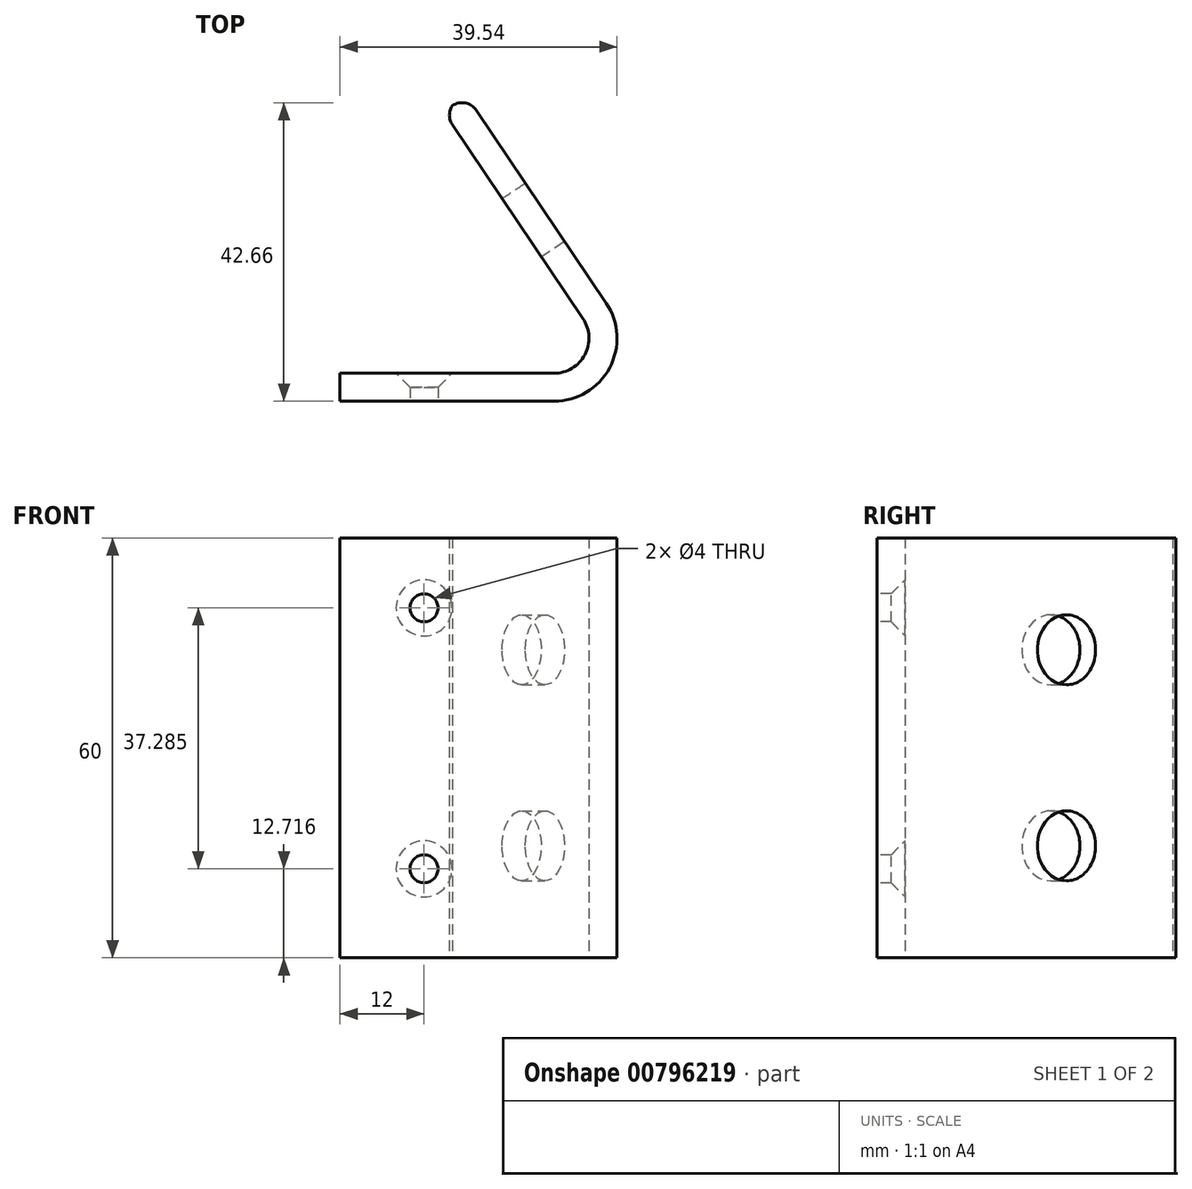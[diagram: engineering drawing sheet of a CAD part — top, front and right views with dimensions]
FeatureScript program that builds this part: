
annotation { "Feature Type Name" : "Feature", "Feature Type Description" : "" }
export const myFeature = defineFeature(function(context is Context, id is Id, definition is map)
    precondition{}
    {
        {
            var Q0;
            Q0=qCreatedBy(makeId("Top.planeOp"),FACE);
            var sketch = newSketch(context, id + "F0", { "sketchPlane" : qUnion([Q0])});
            skLineSegment(sketch, "E0", {"start": v(0, 0) * mm, "end": v(30.54, 0) * mm});
            skLineSegment(sketch, "E1", {"start": v(38.01, 14.02) * mm, "end": v(18.1, 43.63) * mm});
            skLineSegment(sketch, "E2", {"start": v(18.1, 43.63) * mm, "end": v(14.77, 41.4) * mm});
            skLineSegment(sketch, "E3", {"start": v(14.77, 41.4) * mm, "end": v(33.04, 14.25) * mm});
            skLineSegment(sketch, "E4", {"start": v(30.54, 4) * mm, "end": v(0, 4) * mm});
            skLineSegment(sketch, "E5", {"start": v(0, 4) * mm, "end": v(0, 0) * mm});
            skLineSegment(sketch, "E6", {"start": v(34.7, 11.8) * mm, "end": v(33.04, 14.25) * mm});
            skArc(sketch, "E7.filletArc", {"start": v(30.54, 4) * mm, "mid": v(34.96, 6.65) * mm, "end": v(34.7, 11.8) * mm});
            skPoint(sketch, "E8.visualSharp", {"position": v(45.54, 2.83) * mm});
            skPoint(sketch, "E9.visualSharp", {"position": v(50, 0) * mm});
            skPoint(sketch, "E10.newPointA", {"position": v(44.89, 3.8) * mm});
            skArc(sketch, "E10.filletArc", {"start": v(30.54, 0) * mm, "mid": v(38.49, 4.77) * mm, "end": v(38.01, 14.02) * mm});
            skSolve(sketch);
        }
        {
            var Q0;
            Q0=makeQuery(id+"F0.imprint","IMPRINT",FACE,{"disambiguationData":[TD([[makeQuery(id+"F0.imprint","IMPRINT",EDGE,{"derivedFrom":sQuery(id+"F0.wireOp",EDGE,"E0")}),1.0]])]});
            extrude(context, id + "F1", {"entities" : qUnion([Q0]), "depth" : 60 * mm, "offsetDistance" : 25 * mm});
        }
        {
            var Q0;
            Q0=makeQuery(id+"F1.opExtrude","SWEPT_FACE",FACE,{"disambiguationData":[OSD([sQuery(id+"F0.wireOp",EDGE,"E1")])]});
            var sketch = newSketch(context, id + "F2", { "sketchPlane" : qUnion([Q0])});
            skLineSegment(sketch, "E11", {"start": v(6.1, -8.7) * mm, "end": v(6.1, 93.82) * mm, "construction": true});
            skLineSegment(sketch, "E12", {"start": v(41.86, 44) * mm, "end": v(0, 44) * mm, "construction": true});
            skLineSegment(sketch, "E13", {"start": v(40.3, 16) * mm, "end": v(0, 16) * mm, "construction": true});
            skCircle(sketch, "E14", {"center": v(6.1, 44) * mm, "radius": 5 * mm});
            skCircle(sketch, "E15", {"center": v(6.1, 16) * mm, "radius": 5 * mm});
            skSolve(sketch);
        }
        {
            var Q0;
            Q0=makeQuery(id+"F2.imprint","IMPRINT",FACE,{"disambiguationData":[TD([[makeQuery(id+"F2.imprint","IMPRINT",EDGE,{"derivedFrom":sQuery(id+"F2.wireOp",EDGE,"E14")}),1.0]])]});
            var Q1;
            Q1=makeQuery(id+"F2.imprint","IMPRINT",FACE,{"disambiguationData":[TD([[makeQuery(id+"F2.imprint","IMPRINT",EDGE,{"derivedFrom":sQuery(id+"F2.wireOp",EDGE,"E15")}),1.0]])]});
            extrude(context, id + "F3", {"entities" : qUnion([Q0, Q1]), "operationType" : NewBodyOperationType.REMOVE, "oppositeDirection" : true, "depth" : 25 * mm, "offsetDistance" : 25 * mm});
        }
        {
            var Q0;
            Q0=makeQuery(id+"F1.opExtrude","SWEPT_FACE",FACE,{"disambiguationData":[OSD([sQuery(id+"F0.wireOp",EDGE,"E0")])]});
            var sketch = newSketch(context, id + "F4", { "sketchPlane" : qUnion([Q0])});
            skLineSegment(sketch, "E16", {"start": v(12, 65.3) * mm, "end": v(12, -5.47) * mm, "construction": true});
            skLineSegment(sketch, "E17", {"start": v(0, 30) * mm, "end": v(30.54, 30) * mm, "construction": true});
            skLineSegment(sketch, "E18", {"start": v(0, 50) * mm, "end": v(30.54, 50) * mm, "construction": true});
            skCircle(sketch, "E19", {"center": v(12, 50) * mm, "radius": 2 * mm});
            skLineSegment(sketch, "E20", {"start": v(0, 12.72) * mm, "end": v(30.54, 12.72) * mm, "construction": true});
            skCircle(sketch, "E21", {"center": v(12, 12.72) * mm, "radius": 2 * mm});
            skSolve(sketch);
        }
        {
            var Q0;
            Q0=makeQuery(id+"F4.imprint","IMPRINT",FACE,{"disambiguationData":[TD([[makeQuery(id+"F4.imprint","IMPRINT",EDGE,{"derivedFrom":sQuery(id+"F4.wireOp",EDGE,"E21")}),1.0]])]});
            var Q1;
            Q1=makeQuery(id+"F4.imprint","IMPRINT",FACE,{"disambiguationData":[TD([[makeQuery(id+"F4.imprint","IMPRINT",EDGE,{"derivedFrom":sQuery(id+"F4.wireOp",EDGE,"E19")}),1.0]])]});
            extrude(context, id + "F5", {"entities" : qUnion([Q0, Q1]), "operationType" : NewBodyOperationType.REMOVE, "oppositeDirection" : true, "depth" : 25 * mm, "offsetDistance" : 25 * mm});
        }
        {
            var Q0;
            Q0=makeQuery(id+"F5.boolean.opBoolean","INTERSECT",EDGE,{"derivedFrom":[makeQuery(id+"F1.opExtrude","SWEPT_FACE",FACE,{"disambiguationData":[OSD([sQuery(id+"F0.wireOp",EDGE,"E4")])]}),makeQuery(id+"F5.opExtrude","SWEPT_FACE",FACE,{"disambiguationData":[OSD([sQuery(id+"F4.wireOp",EDGE,"E21")])]})]});
            chamfer(context, id + "F6", {"entities" : qUnion([Q0]), "width" : 2 * mm, "tangentPropagation" : true});
        }
        {
            var Q0;
            Q0=makeQuery(id+"F5.boolean.opBoolean","INTERSECT",EDGE,{"derivedFrom":[makeQuery(id+"F1.opExtrude","SWEPT_FACE",FACE,{"disambiguationData":[OSD([sQuery(id+"F0.wireOp",EDGE,"E4")])]}),makeQuery(id+"F5.opExtrude","SWEPT_FACE",FACE,{"disambiguationData":[OSD([sQuery(id+"F4.wireOp",EDGE,"E19")])]})]});
            chamfer(context, id + "F7", {"entities" : qUnion([Q0]), "width" : 2 * mm, "tangentPropagation" : true});
        }
        {
            var Q0;
            Q0=makeQuery(id+"F1.opExtrude","SWEPT_EDGE",EDGE,{"disambiguationData":[OSD([sQuery(id+"F0.wireOp",EDGE,"E1"),sQuery(id+"F0.wireOp",EDGE,"E2")])]});
            fillet(context, id + "F8", {"entities" : qUnion([Q0]), "radius" : 2.5 * mm, "tangentPropagation" : true, "allowEdgeOverflow" : false});
        }
        {
            var Q0;
            Q0=makeQuery(id+"F1.opExtrude","SWEPT_EDGE",EDGE,{"disambiguationData":[OSD([sQuery(id+"F0.wireOp",EDGE,"E2"),sQuery(id+"F0.wireOp",EDGE,"E3")])]});
            fillet(context, id + "F9", {"entities" : qUnion([Q0]), "radius" : 2.5 * mm, "tangentPropagation" : true, "allowEdgeOverflow" : false});
        }
    });
